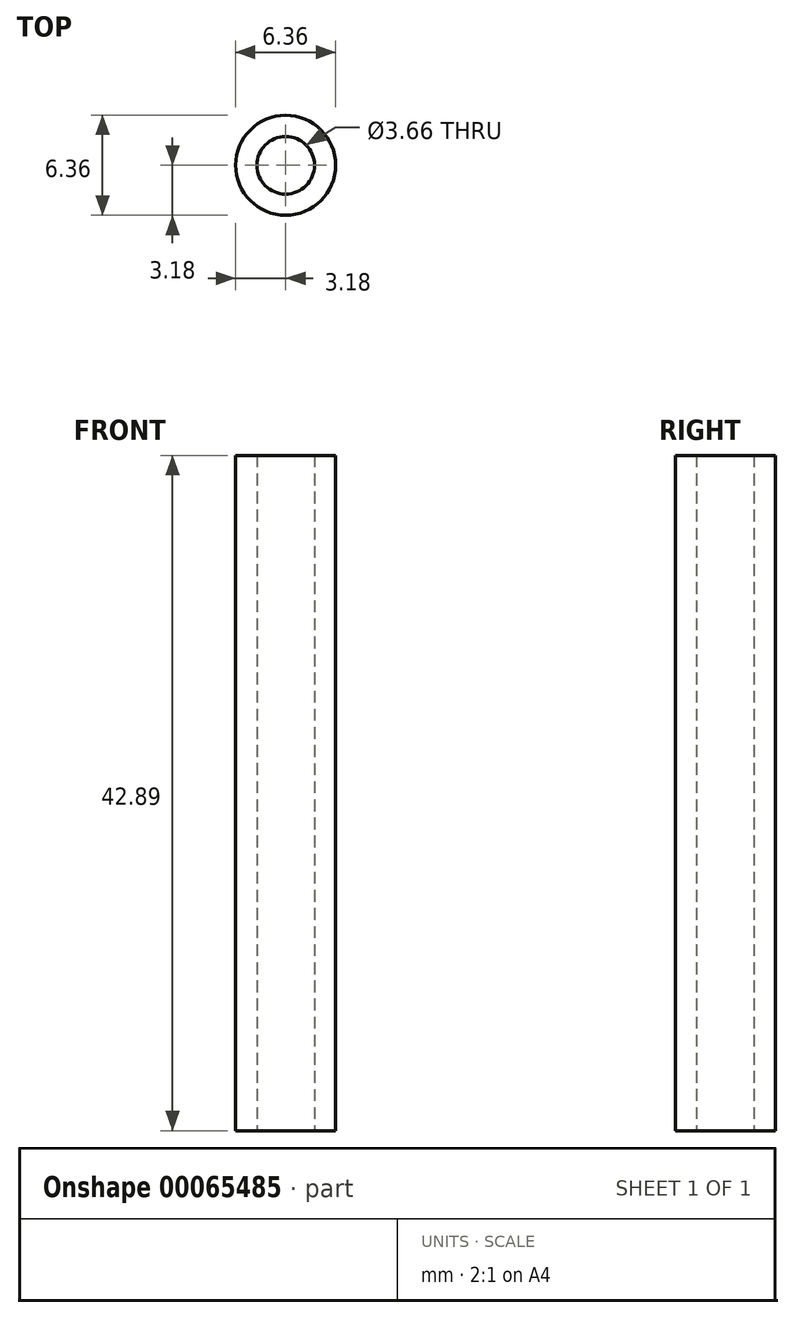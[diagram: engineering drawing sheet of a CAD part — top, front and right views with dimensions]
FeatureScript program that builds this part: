
annotation { "Feature Type Name" : "Feature", "Feature Type Description" : "" }
export const myFeature = defineFeature(function(context is Context, id is Id, definition is map)
    precondition{}
    {
        {
            var Q0;
            Q0=qCreatedBy(makeId("Top.planeOp"),FACE);
            var sketch = newSketch(context, id + "F0", { "sketchPlane" : qUnion([Q0])});
            skCircle(sketch, "E0", {"center": v(0, 0) * mm, "radius": 1.83 * mm});
            skCircle(sketch, "E1", {"center": v(0, 0) * mm, "radius": 3.18 * mm});
            skSolve(sketch);
        }
        {
            var Q0;
            Q0 = qSketchRegion(id + "F0", true);
            extrude(context, id + "F1", {"entities" : qUnion([Q0]), "depth" : 50.8 * mm});
        }
        {
            var Q0;
            Q0=makeQuery(id+"F1.opExtrude","CAP_FACE",FACE,{"disambiguationData":[OSD([sQuery(id+"F0.wireOp",EDGE,"E0"),sQuery(id+"F0.wireOp",EDGE,"E1")])],"isStart":false});
            extrude(context, id + "F2", {"entities" : qUnion([Q0]), "operationType" : NewBodyOperationType.REMOVE, "oppositeDirection" : true, "depth" : 7.9 * mm});
        }
    });
